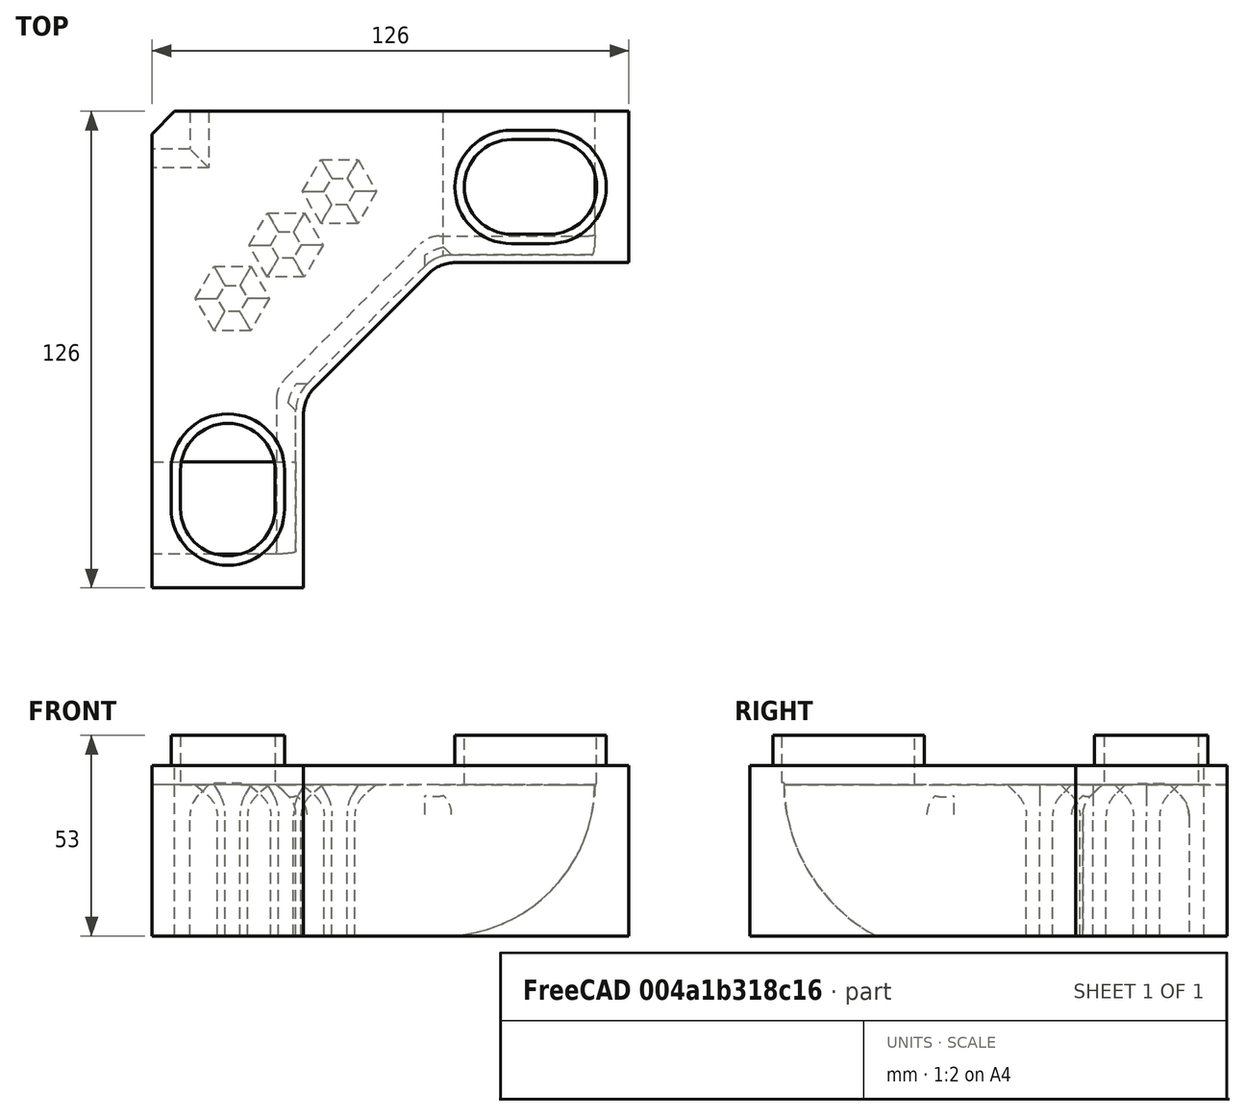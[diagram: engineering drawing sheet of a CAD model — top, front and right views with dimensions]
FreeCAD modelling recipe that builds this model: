
FCSTD DOCUMENT  (FreeCAD 0.19R)
Label: CoryCave
License: All rights reserved
LicenseURL: http://en.wikipedia.org/wiki/All_rights_reserved
objects: Sketcher::SketchObject×8, PartDesign::Fillet×7, PartDesign::Pad×6, PartDesign::Chamfer×3, PartDesign::Pocket×2, PartDesign::Body×1, Mesh::Feature×1
note: 45 computed .brp shape members not serialized (recipe doc carries the construction recipe); baked Part::Feature solids carry a one-line shape summary decoded from their .brp

FEATURE [Sketcher::SketchObject] Sketch
  FullyConstrained = true
  MapMode = 5
  Support = -> [XY_Plane]
  sketch-geometry (8):
    g0: LineSegment StartX=4 StartY=0 StartZ=0 EndX=0 EndY=4 EndZ=0
    g1: LineSegment StartX=0 StartY=4 StartZ=0 EndX=0 EndY=-116 EndZ=0
    g2: LineSegment StartX=0 StartY=-116 StartZ=0 EndX=40 EndY=-116 EndZ=0
    g3: LineSegment StartX=124 StartY=-40 StartZ=0 EndX=124 EndY=0 EndZ=0
    g4: LineSegment StartX=124 StartY=0 StartZ=0 EndX=4 EndY=0 EndZ=0
    g5: LineSegment StartX=40 StartY=-116 StartZ=0 EndX=40 EndY=-74 EndZ=0
    g6: LineSegment StartX=40 StartY=-74 StartZ=0 EndX=74 EndY=-40 EndZ=0
    g7: LineSegment StartX=74 StartY=-40 StartZ=0 EndX=124 EndY=-40 EndZ=0
  constraints (24):
    c: PointOnObject(g0,g-1)
    c: PointOnObject(g0,g-2)
    c: Coincident(g0,g1)
    c: PointOnObject(g1,g-2)
    c: Coincident(g1,g2)
    c: Horizontal(g2)
    c: PointOnObject(g3,g-1)
    c: Vertical(g3)
    c: Coincident(g3,g4)
    c: Coincident(g4,g0)
    c: DistanceX(g0) = 4
    c: DistanceY(g0) = 4
    c: Distance(g1) = 120
    c: Distance(g4) = 120
    c: Distance(g2) = 40
    c: Distance(g3) = 40
    c: Coincident(g2,g5)
    c: Coincident(g5,g6)
    c: Coincident(g6,g7)
    c: Coincident(g7,g3)
    c: Horizontal(g7)
    c: Angle(g6) = 0.785398
    c: Distance(g7) = 50
    c: Vertical(g5)
FEATURE [PartDesign::Pad] Pad
  Direction = (1,1,1)
  Length = 45
  Length2 = 100
  Profile = -> Sketch
  Type = 0
FEATURE [Sketcher::SketchObject] Sketch004
  FullyConstrained = true
  MapMode = 5
  Placement = pos=(0,0,45) rot=(0,0,1;0rad)
  sketch-geometry (8):
    g0: ArcOfCircle CenterX=20 CenterY=-95 CenterZ=0 NormalX=0 NormalY=0 NormalZ=1 AngleXU=0 Radius=15 StartAngle=2e-16 EndAngle=3.14159
    g1: ArcOfCircle CenterX=20 CenterY=-105 CenterZ=0 NormalX=0 NormalY=0 NormalZ=1 AngleXU=0 Radius=15 StartAngle=3.14159 EndAngle=6.28319
    g2: LineSegment StartX=5 StartY=-95 StartZ=0 EndX=5 EndY=-105 EndZ=0
    g3: LineSegment StartX=35 StartY=-95 StartZ=0 EndX=35 EndY=-105 EndZ=0
    g4: ArcOfCircle CenterX=95 CenterY=-20 CenterZ=0 NormalX=0 NormalY=0 NormalZ=1 AngleXU=0 Radius=15 StartAngle=1.5708 EndAngle=4.71239
    g5: ArcOfCircle CenterX=105 CenterY=-20 CenterZ=0 NormalX=0 NormalY=0 NormalZ=1 AngleXU=0 Radius=15 StartAngle=4.71239 EndAngle=7.85398
    g6: LineSegment StartX=95 StartY=-35 StartZ=0 EndX=105 EndY=-35 EndZ=0
    g7: LineSegment StartX=95 StartY=-5 StartZ=0 EndX=105 EndY=-5 EndZ=0
  constraints (20):
    c: Tangent(g0,g3) = 1.5708
    c: Tangent(g0,g2) = -1.5708
    c: Tangent(g2,g1) = -1.5708
    c: Tangent(g3,g1) = 1.5708
    c: Vertical(g2)
    c: Equal(g0,g1)
    c: Distance(g1,g1) = 30
    c: Distance(g3) = 10
    c: Tangent(g4,g7) = 1.5708
    c: Tangent(g4,g6) = -1.5708
    c: Tangent(g6,g5) = -1.5708
    c: Tangent(g7,g5) = 1.5708
    c: Horizontal(g6)
    c: Equal(g4,g5)
    c: Distance(g6) = 10
    c: Distance(g5,g5) = 30
    c: DistanceY(g0) = -95
    c: DistanceX(g4) = 95
    c: DistanceY(g4) = -20
    c: DistanceX(g0) = 20
FEATURE [Sketcher::SketchObject] Sketch010
  FullyConstrained = false
  MapMode = 5
  Placement = pos=(0,0,0) rot=(1,0,0;3.14159rad)
  Support = -> [Pad]
  sketch-geometry (32):
    g0: LineSegment StartX=-11.66 StartY=124 StartZ=0 EndX=38 EndY=124 EndZ=0
    g1: LineSegment StartX=38 StartY=124 StartZ=0 EndX=38 EndY=75 EndZ=0
    g2: LineSegment StartX=38 StartY=75 StartZ=0 EndX=75 EndY=38 EndZ=0
    g3: LineSegment StartX=75 StartY=38 StartZ=0 EndX=124 EndY=38 EndZ=0
    g4: LineSegment StartX=124 StartY=38 StartZ=0 EndX=124 EndY=-8.09 EndZ=0
    g5: LineSegment StartX=124 StartY=-8.09 StartZ=0 EndX=10 EndY=-8.09 EndZ=0
    g6: LineSegment StartX=10 StartY=-8.09 StartZ=0 EndX=10 EndY=10 EndZ=0
    g7: LineSegment StartX=10 StartY=10 StartZ=0 EndX=-11.66 EndY=10 EndZ=0
    g8: LineSegment StartX=-11.66 StartY=10 StartZ=0 EndX=-11.66 EndY=124 EndZ=0
    g9: LineSegment StartX=23.2132 StartY=46.0334 StartZ=0 EndX=25.2132 EndY=49.4975 EndZ=0
    g10: LineSegment StartX=25.2132 StartY=49.4975 StartZ=0 EndX=23.2132 EndY=52.9616 EndZ=0
    g11: LineSegment StartX=23.2132 StartY=52.9616 StartZ=0 EndX=19.2132 EndY=52.9616 EndZ=0
    g12: LineSegment StartX=19.2132 StartY=52.9616 StartZ=0 EndX=17.2132 EndY=49.4975 EndZ=0
    g13: LineSegment StartX=17.2132 StartY=49.4975 StartZ=0 EndX=19.2132 EndY=46.0334 EndZ=0
    g14: LineSegment StartX=19.2132 StartY=46.0334 StartZ=0 EndX=23.2132 EndY=46.0334 EndZ=0
    g15: Circle CenterX=21.2132 CenterY=49.4975 CenterZ=0 NormalX=0 NormalY=0 NormalZ=1 AngleXU=0 Radius=4
    g16: LineSegment StartX=37.3553 StartY=31.8912 StartZ=0 EndX=39.3553 EndY=35.3553 EndZ=0
    g17: LineSegment StartX=39.3553 StartY=35.3553 StartZ=0 EndX=37.3553 EndY=38.8194 EndZ=0
    g18: LineSegment StartX=37.3553 StartY=38.8194 StartZ=0 EndX=33.3553 EndY=38.8194 EndZ=0
    g19: LineSegment StartX=33.3553 StartY=38.8194 StartZ=0 EndX=31.3553 EndY=35.3553 EndZ=0
    g20: LineSegment StartX=31.3553 StartY=35.3553 StartZ=0 EndX=33.3553 EndY=31.8912 EndZ=0
    g21: LineSegment StartX=33.3553 StartY=31.8912 StartZ=0 EndX=37.3553 EndY=31.8912 EndZ=0
    g22: Circle CenterX=35.3553 CenterY=35.3553 CenterZ=0 NormalX=0 NormalY=0 NormalZ=1 AngleXU=0 Radius=4
    g23: LineSegment StartX=51.4975 StartY=17.7491 StartZ=0 EndX=53.4975 EndY=21.2132 EndZ=0
    g24: LineSegment StartX=53.4975 StartY=21.2132 StartZ=0 EndX=51.4975 EndY=24.6773 EndZ=0
    g25: LineSegment StartX=51.4975 StartY=24.6773 StartZ=0 EndX=47.4975 EndY=24.6773 EndZ=0
    g26: LineSegment StartX=47.4975 StartY=24.6773 StartZ=0 EndX=45.4975 EndY=21.2132 EndZ=0
    g27: LineSegment StartX=45.4975 StartY=21.2132 StartZ=0 EndX=47.4975 EndY=17.7491 EndZ=0
    g28: LineSegment StartX=47.4975 StartY=17.7491 StartZ=0 EndX=51.4975 EndY=17.7491 EndZ=0
    g29: Circle CenterX=49.4975 CenterY=21.2132 CenterZ=0 NormalX=0 NormalY=0 NormalZ=1 AngleXU=0 Radius=4
    g30: LineSegment StartX=-11.66 StartY=82.3707 StartZ=0 EndX=100.464 EndY=-29.7535 EndZ=0
    g31: LineSegment StartX=0 StartY=0 StartZ=0 EndX=89.066 EndY=89.066 EndZ=0
  constraints (83):
    c: Horizontal(g0)
    c: Coincident(g0,g1)
    c: Vertical(g1)
    c: Coincident(g1,g2)
    c: Coincident(g2,g3)
    c: Horizontal(g3)
    c: Coincident(g3,g4)
    c: Vertical(g4)
    c: Coincident(g4,g5)
    c: Coincident(g5,g6)
    c: Vertical(g6)
    c: Coincident(g6,g7)
    c: Horizontal(g7)
    c: Coincident(g7,g8)
    c: Coincident(g8,g0)
    c: Vertical(g8)
    c: DistanceY(g0) = 124
    c: DistanceX(g3) = 124
    c: DistanceX(g0) = 38
    c: DistanceY(g3) = 38
    c: Angle(g2) = -0.785398
    c: DistanceX(g2) = 75
    c: DistanceX(g6) = 10
    c: DistanceY(g6) = 10
    c: DistanceX(g0) = -11.66
    c: DistanceY(g5) = -8.09
    c: Horizontal(g5)
    c: Coincident(g9,g10)
    c: Coincident(g10,g11)
    c: Coincident(g11,g12)
    c: Coincident(g12,g13)
    c: Coincident(g13,g14)
    c: Coincident(g14,g9)
    c: Equal(g9, g10-g14) x5
    c: PointOnObject(g9,g15)
    c: PointOnObject(g10,g15)
    c: PointOnObject(g11,g15)
    c: PointOnObject(g12,g15)
    c: PointOnObject(g13,g15)
    c: PointOnObject(g14,g15)
    c: Coincident(g16,g17)
    c: Coincident(g17,g18)
    c: Coincident(g18,g19)
    c: Coincident(g19,g20)
    c: Coincident(g20,g21)
    c: Coincident(g21,g16)
    c: Equal(g16, g17-g21) x5
    c: PointOnObject(g16,g22)
    c: PointOnObject(g17,g22)
    c: PointOnObject(g18,g22)
    c: PointOnObject(g19,g22)
    c: PointOnObject(g20,g22)
    c: PointOnObject(g21,g22)
    c: Coincident(g23,g24)
    c: Coincident(g24,g25)
    c: Coincident(g25,g26)
    c: Coincident(g26,g27)
    c: Coincident(g27,g28)
    c: Coincident(g28,g23)
    c: Equal(g23, g24-g28) x5
    c: PointOnObject(g23,g29)
    c: PointOnObject(g24,g29)
    c: PointOnObject(g25,g29)
    c: PointOnObject(g26,g29)
    c: PointOnObject(g27,g29)
    c: PointOnObject(g28,g29)
    c: Diameter(g29) = 8
    c: Equal(g29,g22)
    c: Equal(g29,g15)
    c: Horizontal(g11)
    c: Horizontal(g18)
    c: Horizontal(g25)
    c: PointOnObject(g30,g8)
    c: PointOnObject(g29,g30)
    c: PointOnObject(g22,g30)
    c: PointOnObject(g15,g30)
    c: Distance(g15,g22) = 20
    c: Distance(g22,g29) = 20
    c: Angle(g30) = -0.785398
    c: Coincident(g31,g-1)
    c: Angle(g31) = 0.785398
    c: PointOnObject(g22,g31)
    c: Distance(g-1,g22) = 50
FEATURE [PartDesign::Pocket] Pocket
  BaseFeature = -> Pad
  Length = 40
  Length2 = 100
  Profile = -> Sketch010
  Type = 0
FEATURE [PartDesign::Chamfer] Chamfer
  Angle = 45
  Base = -> Pocket [Edge42,Edge43,Edge41,Edge40,Edge36]
  BaseFeature = -> Pocket
  ChamferType = 0
  FlipDirection = false
  Size = 5
  Size2 = 1
  SupportTransform = false
FEATURE [PartDesign::Fillet] Fillet
  Base = -> Chamfer [Edge75,Edge76,Edge78,Edge65,Edge10]
  BaseFeature = -> Chamfer
  Radius = 7
  SupportTransform = false
FEATURE [PartDesign::Fillet] Fillet001
  Base = -> Fillet [Edge79,Edge13]
  BaseFeature = -> Fillet
  Radius = 5
  SupportTransform = false
FEATURE [PartDesign::Fillet] Fillet002
  Base = -> Fillet001 [Edge87,Edge35]
  BaseFeature = -> Fillet001
  Radius = 10
  SupportTransform = false
FEATURE [PartDesign::Fillet] Fillet003
  Base = -> Fillet002 [Edge48,Edge44]
  BaseFeature = -> Fillet002
  Radius = 10
  SupportTransform = false
FEATURE [PartDesign::Chamfer] Chamfer001
  Angle = 45
  Base = -> Fillet003 [Edge78,Edge80]
  BaseFeature = -> Fillet003
  ChamferType = 0
  FlipDirection = false
  Size = 5
  Size2 = 1
  SupportTransform = false
FEATURE [PartDesign::Fillet] Fillet004
  Base = -> Chamfer001 [Edge83,Edge43]
  BaseFeature = -> Chamfer001
  Radius = 8
  SupportTransform = false
FEATURE [PartDesign::Chamfer] Chamfer002
  Angle = 45
  Base = -> Fillet004 [Edge31,Edge37,Edge43,Edge41,Edge45,Edge35,Edge39,Edge29,Edge33,Edge30,Edge36,Edge42,Edge44,Edge38,Edge32,Edge34,Edge40,Edge46]
  BaseFeature = -> Fillet004
  ChamferType = 0
  FlipDirection = false
  Size = 5
  Size2 = 1
  SupportTransform = false
FEATURE [PartDesign::Fillet] Fillet005
  Base = -> Chamfer002 [Edge41,Edge43,Edge95,Edge97,Edge107,Edge109,Edge40,Edge36,Edge90,Edge94,Edge106,Edge102,Edge99,Edge87,Edge33,Edge103,Edge91,Edge37]
  BaseFeature = -> Chamfer002
  Radius = 8
  SupportTransform = false
FEATURE [Sketcher::SketchObject] Sketch006
  FullyConstrained = true
  MapMode = 5
  Placement = pos=(0,0,53) rot=(0,0,1;0rad)
  sketch-geometry (8):
    g0: ArcOfCircle CenterX=95 CenterY=-20 CenterZ=0 NormalX=0 NormalY=0 NormalZ=1 AngleXU=0 Radius=12.5 StartAngle=1.5708 EndAngle=4.71239
    g1: ArcOfCircle CenterX=105 CenterY=-20 CenterZ=0 NormalX=0 NormalY=0 NormalZ=1 AngleXU=0 Radius=12.5 StartAngle=4.71239 EndAngle=7.85398
    g2: LineSegment StartX=95 StartY=-32.5 StartZ=0 EndX=105 EndY=-32.5 EndZ=0
    g3: LineSegment StartX=95 StartY=-7.5 StartZ=0 EndX=105 EndY=-7.5 EndZ=0
    g4: ArcOfCircle CenterX=20 CenterY=-95 CenterZ=0 NormalX=0 NormalY=0 NormalZ=1 AngleXU=0 Radius=12.5 StartAngle=-9e-16 EndAngle=3.14159
    g5: ArcOfCircle CenterX=20 CenterY=-105 CenterZ=0 NormalX=0 NormalY=0 NormalZ=1 AngleXU=0 Radius=12.5 StartAngle=3.14159 EndAngle=6.28319
    g6: LineSegment StartX=7.5 StartY=-95 StartZ=0 EndX=7.5 EndY=-105 EndZ=0
    g7: LineSegment StartX=32.5 StartY=-95 StartZ=0 EndX=32.5 EndY=-105 EndZ=0
  constraints (20):
    c: Tangent(g0,g3) = 1.5708
    c: Tangent(g0,g2) = -1.5708
    c: Tangent(g2,g1) = -1.5708
    c: Tangent(g3,g1) = 1.5708
    c: Horizontal(g2)
    c: Equal(g0,g1)
    c: Tangent(g4,g7) = 1.5708
    c: Tangent(g4,g6) = -1.5708
    c: Tangent(g6,g5) = -1.5708
    c: Tangent(g7,g5) = 1.5708
    c: Vertical(g6)
    c: Equal(g4,g5)
    c: Distance(g4,g4) = 25
    c: Distance(g7) = 10
    c: Distance(g1,g1) = 25
    c: Distance(g3) = 10
    c: DistanceY(g1) = -20
    c: DistanceX(g4) = 20
    c: DistanceY(g4) = -95
    c: DistanceX(g0) = 95
FEATURE [PartDesign::Pad] Pad001
  BaseFeature = -> Fillet005
  Direction = (1,1,1)
  Length = 8
  Length2 = 100
  Profile = -> Sketch004
  Type = 0
FEATURE [PartDesign::Pocket] Pocket001
  BaseFeature = -> Pad001
  Length = 5
  Length2 = 100
  Profile = -> Sketch006
  Type = 1
FEATURE [Sketcher::SketchObject] Sketch011
  FullyConstrained = false
  MapMode = 5
  Placement = pos=(0,0,0) rot=(0,0.707107,0.707107;3.14159rad)
  Support = -> [Pocket001]
  sketch-geometry (4):
    g0: LineSegment StartX=-124.707 StartY=40.2 StartZ=0 EndX=-124.707 EndY=0 EndZ=0
    g1: LineSegment StartX=-124.707 StartY=0 StartZ=0 EndX=-76.8 EndY=0 EndZ=0
    g2: ArcOfCircle CenterX=-76.8 CenterY=40.2 CenterZ=0 NormalX=0 NormalY=0 NormalZ=1 AngleXU=0 Radius=40.2 StartAngle=3.14159 EndAngle=4.71239
    g3: LineSegment StartX=-117 StartY=40.2 StartZ=0 EndX=-124.707 EndY=40.2 EndZ=0
  constraints (11):
    c: PointOnObject(g0,g-1)
    c: Vertical(g0)
    c: Coincident(g0,g1)
    c: Horizontal(g1)
    c: Tangent(g2,g1) = -1.5708
    c: Coincident(g3,g2)
    c: Coincident(g3,g0)
    c: Horizontal(g3)
    c: Perpendicular(g2,g3)
    c: DistanceY(g2) = 40.2
    c: DistanceX(g2) = -117
FEATURE [PartDesign::Pad] Pad002
  BaseFeature = -> Pocket001
  Direction = (1,1,1)
  Length = 39
  Length2 = 100
  Profile = -> Sketch011
  Reversed = true
  Type = 0
FEATURE [Sketcher::SketchObject] Sketch012
  FullyConstrained = true
  MapMode = 5
  Placement = pos=(0,0,0) rot=(0.57735,-0.57735,-0.57735;2.0944rad)
  Support = -> [Pad002]
  sketch-geometry (4):
    g0: ArcOfCircle CenterX=76.8 CenterY=40.2 CenterZ=0 NormalX=0 NormalY=0 NormalZ=1 AngleXU=0 Radius=40.2 StartAngle=4.71239 EndAngle=6.28319
    g1: LineSegment StartX=76.8 StartY=0 StartZ=0 EndX=125 EndY=0 EndZ=0
    g2: LineSegment StartX=125 StartY=0 StartZ=0 EndX=125 EndY=40.2 EndZ=0
    g3: LineSegment StartX=125 StartY=40.2 StartZ=0 EndX=117 EndY=40.2 EndZ=0
  constraints (12):
    c: Coincident(g1,g2)
    c: Vertical(g2)
    c: Coincident(g2,g3)
    c: Coincident(g3,g0)
    c: Horizontal(g3)
    c: Horizontal(g1)
    c: PointOnObject(g1,g-1)
    c: Perpendicular(g0,g3)
    c: DistanceX(g0) = 117
    c: DistanceY(g0) = 40.2
    c: DistanceX(g1) = 125
    c: Tangent(g0,g1) = -1.5708
FEATURE [PartDesign::Pad] Pad003
  BaseFeature = -> Pad002
  Direction = (1,1,1)
  Length = 39
  Length2 = 100
  Profile = -> Sketch012
  Reversed = true
  Type = 0
FEATURE [Sketcher::SketchObject] Sketch013
  FullyConstrained = true
  MapMode = 5
  Placement = pos=(0,0,0) rot=(1,0,0;3.14159rad)
  Support = -> [Pad003]
  sketch-geometry (8):
    g0: LineSegment StartX=0 StartY=120 StartZ=0 EndX=0 EndY=7 EndZ=0
    g1: LineSegment StartX=0 StartY=7 StartZ=0 EndX=7 EndY=-9e-16 EndZ=0
    g2: LineSegment StartX=7 StartY=-9e-16 StartZ=0 EndX=120 EndY=0 EndZ=0
    g3: LineSegment StartX=75 StartY=39.5 StartZ=0 EndX=39.5 EndY=75 EndZ=0
    g4: LineSegment StartX=39.5 StartY=75 StartZ=0 EndX=39.5 EndY=120 EndZ=0
    g5: LineSegment StartX=39.5 StartY=120 StartZ=0 EndX=0 EndY=120 EndZ=0
    g6: LineSegment StartX=75 StartY=39.5 StartZ=0 EndX=120 EndY=39.5 EndZ=0
    g7: LineSegment StartX=120 StartY=39.5 StartZ=0 EndX=120 EndY=0 EndZ=0
  constraints (24):
    c: PointOnObject(g0,g-2)
    c: PointOnObject(g0,g-2)
    c: Coincident(g0,g1)
    c: PointOnObject(g1,g-1)
    c: Coincident(g1,g2)
    c: PointOnObject(g2,g-1)
    c: Coincident(g3,g4)
    c: Vertical(g4)
    c: Coincident(g4,g5)
    c: Coincident(g5,g0)
    c: Coincident(g3,g6)
    c: Horizontal(g6)
    c: Coincident(g6,g7)
    c: Coincident(g7,g2)
    c: DistanceY(g0) = 120
    c: Horizontal(g5)
    c: DistanceX(g4) = 39.5
    c: Angle(g3) = 2.35619
    c: DistanceY(g3) = 75
    c: DistanceX(g3) = 75
    c: DistanceX(g6) = 120
    c: Vertical(g7)
    c: DistanceY(g0) = 7
    c: DistanceX(g1) = 7
FEATURE [PartDesign::Pad] Pad004
  BaseFeature = -> Pad003
  Direction = (1,1,1)
  Length = 1
  Length2 = 100
  Profile = -> Sketch013
  Reversed = true
  Type = 0
FEATURE [PartDesign::Fillet] Fillet006
  Base = -> Pad004 [Edge114,Edge81,Edge177,Edge176,Edge174]
  BaseFeature = -> Pad004
  Radius = 3
  SupportTransform = false
FEATURE [Sketcher::SketchObject] Sketch014
  FullyConstrained = false
  MapMode = 5
  Placement = pos=(0,0,40) rot=(1,0,0;3.14159rad)
  Support = -> [Fillet006]
  sketch-geometry (8):
    g0: LineSegment StartX=4.88122 StartY=119.649 StartZ=0 EndX=34.4345 EndY=119.649 EndZ=0
    g1: LineSegment StartX=34.4345 StartY=119.649 StartZ=0 EndX=34.4345 EndY=81.0748 EndZ=0
    g2: LineSegment StartX=34.4345 StartY=81.0748 StartZ=0 EndX=4.88122 EndY=81.0748 EndZ=0
    g3: LineSegment StartX=4.88122 StartY=81.0748 StartZ=0 EndX=4.88122 EndY=119.649 EndZ=0
    g4: LineSegment StartX=77.9797 StartY=34.4198 StartZ=0 EndX=121.171 EndY=34.4198 EndZ=0
    g5: LineSegment StartX=121.171 StartY=34.4198 StartZ=0 EndX=121.171 EndY=5.07034 EndZ=0
    g6: LineSegment StartX=121.171 StartY=5.07034 StartZ=0 EndX=77.9797 EndY=5.07034 EndZ=0
    g7: LineSegment StartX=77.9797 StartY=5.07034 StartZ=0 EndX=77.9797 EndY=34.4198 EndZ=0
  constraints (16):
    c: Coincident(g0,g1)
    c: Coincident(g1,g2)
    c: Coincident(g2,g3)
    c: Coincident(g3,g0)
    c: Horizontal(g0)
    c: Horizontal(g2)
    c: Vertical(g1)
    c: Vertical(g3)
    c: Coincident(g4,g5)
    c: Coincident(g5,g6)
    c: Coincident(g6,g7)
    c: Coincident(g7,g4)
    c: Horizontal(g4)
    c: Horizontal(g6)
    c: Vertical(g5)
    c: Vertical(g7)
FEATURE [PartDesign::Pad] Pad005
  BaseFeature = -> Fillet006
  Direction = (1,1,1)
  Length = 0.3
  Length2 = 100
  Profile = -> Sketch014
  Reversed = true
  Type = 0
FEATURE [PartDesign::Body] Body
  Group = -> [Sketch,Pad,Sketch004,Sketch006,Sketch010,Pocket,Chamfer,Fillet,Fillet001,Fillet002,Fillet003,Chamfer001,Fillet004,Chamfer002,Fillet005,Pad001,Pocket001,Sketch011,Pad002,Sketch012,Pad003,Sketch013,Pad004,Fillet006,Sketch014,Pad005]
  Origin = -> Origin
  Tip = -> Pad005
FEATURE [Mesh::Feature] Mesh  label="Pad005 (Meshed)"
